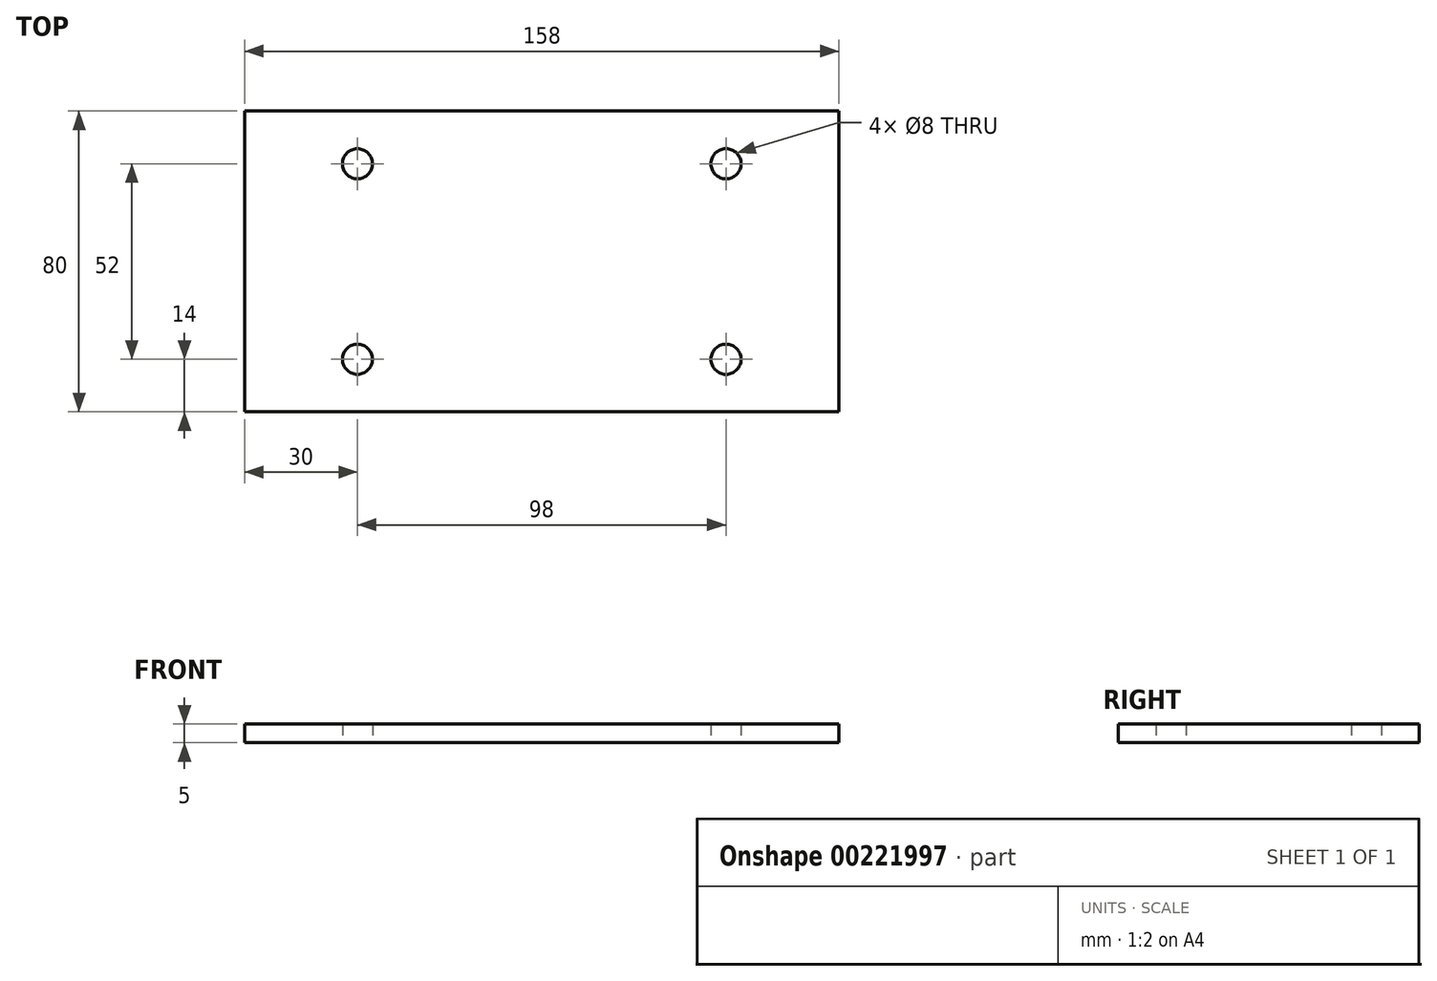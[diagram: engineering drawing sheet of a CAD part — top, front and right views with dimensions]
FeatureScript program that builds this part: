
annotation { "Feature Type Name" : "Feature", "Feature Type Description" : "" }
export const myFeature = defineFeature(function(context is Context, id is Id, definition is map)
    precondition{}
    {
        {
            var Q0;
            Q0=qCreatedBy(makeId("Top.planeOp"),FACE);
            var sketch = newSketch(context, id + "F0", { "sketchPlane" : qUnion([Q0])});
            skLineSegment(sketch, "E0.bottom", {"start": v(79, -40) * mm, "end": v(-79, -40) * mm});
            skLineSegment(sketch, "E0.top", {"start": v(79, 40) * mm, "end": v(-79, 40) * mm});
            skLineSegment(sketch, "E0.left", {"start": v(79, -40) * mm, "end": v(79, 40) * mm});
            skLineSegment(sketch, "E0.right", {"start": v(-79, -40) * mm, "end": v(-79, 40) * mm});
            skPoint(sketch, "E0.middle", {"position": v(0, 0) * mm});
            skCircle(sketch, "E1", {"center": v(49, 26) * mm, "radius": 4 * mm});
            skCircle(sketch, "E2", {"center": v(49, -26) * mm, "radius": 4 * mm});
            skCircle(sketch, "E3", {"center": v(-49, 26) * mm, "radius": 4 * mm});
            skCircle(sketch, "E4", {"center": v(-49, -26) * mm, "radius": 4 * mm});
            skLineSegment(sketch, "E5", {"start": v(49, 40) * mm, "end": v(49, -40) * mm});
            skLineSegment(sketch, "E6", {"start": v(-49, 40) * mm, "end": v(-49, -40) * mm});
            skLineSegment(sketch, "E7", {"start": v(-79, 26) * mm, "end": v(79, 26) * mm});
            skLineSegment(sketch, "E8", {"start": v(-79, -26) * mm, "end": v(79, -26) * mm});
            skSolve(sketch);
        }
        {
            var Q0;
            {var subQ0=sQuery(id+"F0.wireOp",EDGE,"E0.right");var subQ1=sQuery(id+"F0.wireOp",EDGE,"E0.top");var subQ2=makeQuery(id+"F0.imprint","INTERSECT",VERTEX,{"derivedFrom":[subQ1,subQ0]});Q0=makeQuery(id+"F0.imprint","IMPRINT",FACE,{"disambiguationData":[TD([[makeQuery(id+"F0.imprint","IMPRINT",EDGE,{"disambiguationData":[TD([[subQ2,1.0]])],"derivedFrom":subQ1}),1.0]])]});}
            var Q1;
            {var subQ7=sQuery(id+"F0.wireOp",EDGE,"E7");var subQ9=sQuery(id+"F0.wireOp",EDGE,"E0.right");var subQ10=makeQuery(id+"F0.imprint","INTERSECT",VERTEX,{"derivedFrom":[subQ9,subQ7]});Q1=makeQuery(id+"F0.imprint","IMPRINT",FACE,{"disambiguationData":[TD([[makeQuery(id+"F0.imprint","IMPRINT",EDGE,{"disambiguationData":[TD([[subQ10,1.0]])],"derivedFrom":subQ9}),-1.0]])]});}
            var Q2;
            {var subQ0=sQuery(id+"F0.wireOp",EDGE,"E7");var subQ10=sQuery(id+"F0.wireOp",EDGE,"E1");var subQ15=makeQuery(id+"F0.imprint","INTERSECT",VERTEX,{"disambiguationData":[OD(1.0)],"derivedFrom":[subQ10,subQ0]});Q2=makeQuery(id+"F0.imprint","IMPRINT",FACE,{"disambiguationData":[TD([[makeQuery(id+"F0.imprint","IMPRINT",EDGE,{"disambiguationData":[TD([[subQ15,-1.0]])],"derivedFrom":subQ10}),-1.0]])]});}
            var Q3;
            {var subQ0=sQuery(id+"F0.wireOp",EDGE,"E5");var subQ1=sQuery(id+"F0.wireOp",EDGE,"E0.top");var subQ2=makeQuery(id+"F0.imprint","INTERSECT",VERTEX,{"derivedFrom":[subQ1,subQ0]});Q3=makeQuery(id+"F0.imprint","IMPRINT",FACE,{"disambiguationData":[TD([[makeQuery(id+"F0.imprint","IMPRINT",EDGE,{"disambiguationData":[TD([[subQ2,-1.0]])],"derivedFrom":subQ1}),1.0]])]});}
            var Q4;
            {var subQ1=sQuery(id+"F0.wireOp",EDGE,"E0.top");var subQ5=sQuery(id+"F0.wireOp",EDGE,"E0.left");var subQ6=makeQuery(id+"F0.imprint","INTERSECT",VERTEX,{"derivedFrom":[subQ1,subQ5]});Q4=makeQuery(id+"F0.imprint","IMPRINT",FACE,{"disambiguationData":[TD([[makeQuery(id+"F0.imprint","IMPRINT",EDGE,{"disambiguationData":[TD([[subQ6,-1.0]])],"derivedFrom":subQ1}),1.0]])]});}
            var Q5;
            {var subQ5=sQuery(id+"F0.wireOp",EDGE,"E7");var subQ6=sQuery(id+"F0.wireOp",EDGE,"E0.left");var subQ7=makeQuery(id+"F0.imprint","INTERSECT",VERTEX,{"derivedFrom":[subQ6,subQ5]});Q5=makeQuery(id+"F0.imprint","IMPRINT",FACE,{"disambiguationData":[TD([[makeQuery(id+"F0.imprint","IMPRINT",EDGE,{"disambiguationData":[TD([[subQ7,1.0]])],"derivedFrom":subQ6}),1.0]])]});}
            var Q6;
            {var subQ1=sQuery(id+"F0.wireOp",EDGE,"E0.bottom");var subQ7=sQuery(id+"F0.wireOp",EDGE,"E0.left");var subQ8=makeQuery(id+"F0.imprint","INTERSECT",VERTEX,{"derivedFrom":[subQ1,subQ7]});Q6=makeQuery(id+"F0.imprint","IMPRINT",FACE,{"disambiguationData":[TD([[makeQuery(id+"F0.imprint","IMPRINT",EDGE,{"disambiguationData":[TD([[subQ8,-1.0]])],"derivedFrom":subQ1}),-1.0]])]});}
            var Q7;
            {var subQ0=sQuery(id+"F0.wireOp",EDGE,"E5");var subQ1=sQuery(id+"F0.wireOp",EDGE,"E0.bottom");var subQ2=makeQuery(id+"F0.imprint","INTERSECT",VERTEX,{"derivedFrom":[subQ1,subQ0]});Q7=makeQuery(id+"F0.imprint","IMPRINT",FACE,{"disambiguationData":[TD([[makeQuery(id+"F0.imprint","IMPRINT",EDGE,{"disambiguationData":[TD([[subQ2,-1.0]])],"derivedFrom":subQ1}),-1.0]])]});}
            var Q8;
            {var subQ1=sQuery(id+"F0.wireOp",EDGE,"E0.bottom");var subQ7=sQuery(id+"F0.wireOp",EDGE,"E0.right");var subQ8=makeQuery(id+"F0.imprint","INTERSECT",VERTEX,{"derivedFrom":[subQ1,subQ7]});Q8=makeQuery(id+"F0.imprint","IMPRINT",FACE,{"disambiguationData":[TD([[makeQuery(id+"F0.imprint","IMPRINT",EDGE,{"disambiguationData":[TD([[subQ8,1.0]])],"derivedFrom":subQ1}),-1.0]])]});}
            extrude(context, id + "F1", {"entities" : qUnion([Q0, Q1, Q2, Q3, Q4, Q5, Q6, Q7, Q8]), "depth" : 5 * mm});
        }
    });
